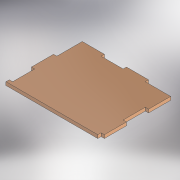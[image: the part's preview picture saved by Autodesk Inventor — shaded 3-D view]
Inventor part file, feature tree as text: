
AUTODESK INVENTOR PART (.ipt)
format: ipt  version: 2018.2 (Build 222227000, 227)  size: 166,912 bytes
history: native  units: mm
features: extrude x1, sketch x1
ambient origin geometry x8: Origin, YZ Plane, XZ Plane, XY Plane, X Axis, Y Axis, Z Axis, Center Point
bodies: Solid1 (feature_tree)
feature tree (2):
  extrude  "Extrusion1"  Depth=3.0mm
  sketch  "Sketch1"  dims[d0=83.0mm d1=3.0mm d2=3.0mm d3=20.0mm d4=20.0mm d5=20.0mm d6=3.0mm d7=20.0mm d8=20.0mm d9=20.0mm d10=20.0mm d11=3.0mm d12=20.0mm d13=3.0mm d14=20.0mm d16=20.0mm d17=3.0mm d18=0.0mm]
